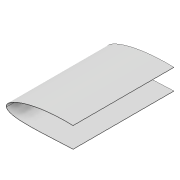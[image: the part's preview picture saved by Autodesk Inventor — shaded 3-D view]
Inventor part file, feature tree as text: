
AUTODESK INVENTOR PART (.ipt)
format: ipt  version: 2022 (Build 260153000, 153)  size: 431,616 bytes
history: native  units: mm
features: extrude x14, sketch x12, projected_geometry x9, plane x4, thicken_offset x1, shell x1, fillet x1
ambient origin geometry x8: Origin, YZ Plane, XZ Plane, XY Plane, X Axis, Y Axis, Z Axis, Center Point
bodies: Solid1 (feature_tree)
feature tree (42):
  extrude  "Extrusion1"  Depth=1.0mm
  thicken_offset  "Thicken1"
  shell  "Shell1"  Thickness=5.215mm
  extrude  "Extrusion23"  Depth=63.6mm
  plane  "Work Plane3"
  sketch  "Sketch26"  dims[d69=4.1mm d70=63.6mm]
  plane  "Work Plane4"
  extrude  "Extrusion9"  Depth=4.2mm
  plane  "Work Plane5"
  sketch  "Sketch38"  dims[d88=2.0mm d89=4.0mm]
  extrude  "Extrusion10"  Depth=6.0mm
  extrude  "Extrusion11"  Depth=21.0mm TaperAngle=0.0deg
  extrude  "Extrusion12"  Depth=5.0mm
  plane  "Work Plane6"
  extrude  "Extrusion13"  Depth=3.0mm TaperAngle=0.0deg
  extrude  "Extrusion15"  Depth=2.0mm
  extrude  "Extrusion16"  Depth=4.0mm
  extrude  "Extrusion17"  Depth=3.0mm TaperAngle=0.0deg
  extrude  "Extrusion20"  Depth=6.5mm TaperAngle=0.0deg
  fillet  "Fillet2"  Radius=28.0mm
  extrude  "Extrusion18"  Depth=200.0mm
  extrude  "Extrusion21"  Depth=100.0mm TaperAngle=0.0deg
  extrude  "Extrusion22"  Depth=7.0mm
  sketch  "Sketch3"  dims[d0=300.0mm d1=0.0mm d2=1.0mm d68=5.215mm]
  sketch  "Sketch27"  dims[d71=16.0mm d72=4.2mm]
  projected_geometry  "Projected Loop13"
  sketch  "Sketch29"  dims[d73=63.6mm d74=6.0mm]
  sketch  "Sketch30"  dims[d75=7.0mm d76=21.0mm d77=0.0mm]
  projected_geometry  "Projected Loop14"
  sketch  "Sketch31"  dims[d78=-11.0mm d79=5.0mm]
  projected_geometry  "Projected Loop15"
  projected_geometry  "Projected Loop16"
  projected_geometry  "Projected Loop17"
  sketch  "Sketch33"  dims[d80=10.0mm d83=3.0mm d84=0.0mm]
  projected_geometry  "Projected Loop18"
  projected_geometry  "Projected Loop19"
  sketch  "Sketch36"  dims[d86=0.65mm d87=2.0mm]
  projected_geometry  "Projected Loop20"
  sketch  "Sketch39"  dims[d90=4.0mm d91=3.0mm d92=0.0mm]
  sketch  "Sketch41"  dims[d93=12.0mm d94=6.5mm d95=0.0mm d96=28.0mm]
  sketch  "Sketch42"  dims[d98=9.0mm d99=0.0mm d103=200.0mm d104=100.0mm d105=0.0mm d106=7.0mm d107=4.1mm d108=7.0mm d109=2.0mm d110=0.0mm d111=2.0mm d112=0.0mm d113=2.0mm d114=95.0mm d115=10.0mm d116=0.0mm d119=100.0mm d120=0.0mm d121=1.0mm d122=3.0mm d123=0.0mm d124=10.0mm d125=0.0mm d126=1.0mm d127=1.0mm d128=200.0mm d129=1000.0mm d130=0.0mm]
  projected_geometry  "Project Cut Edges1"
